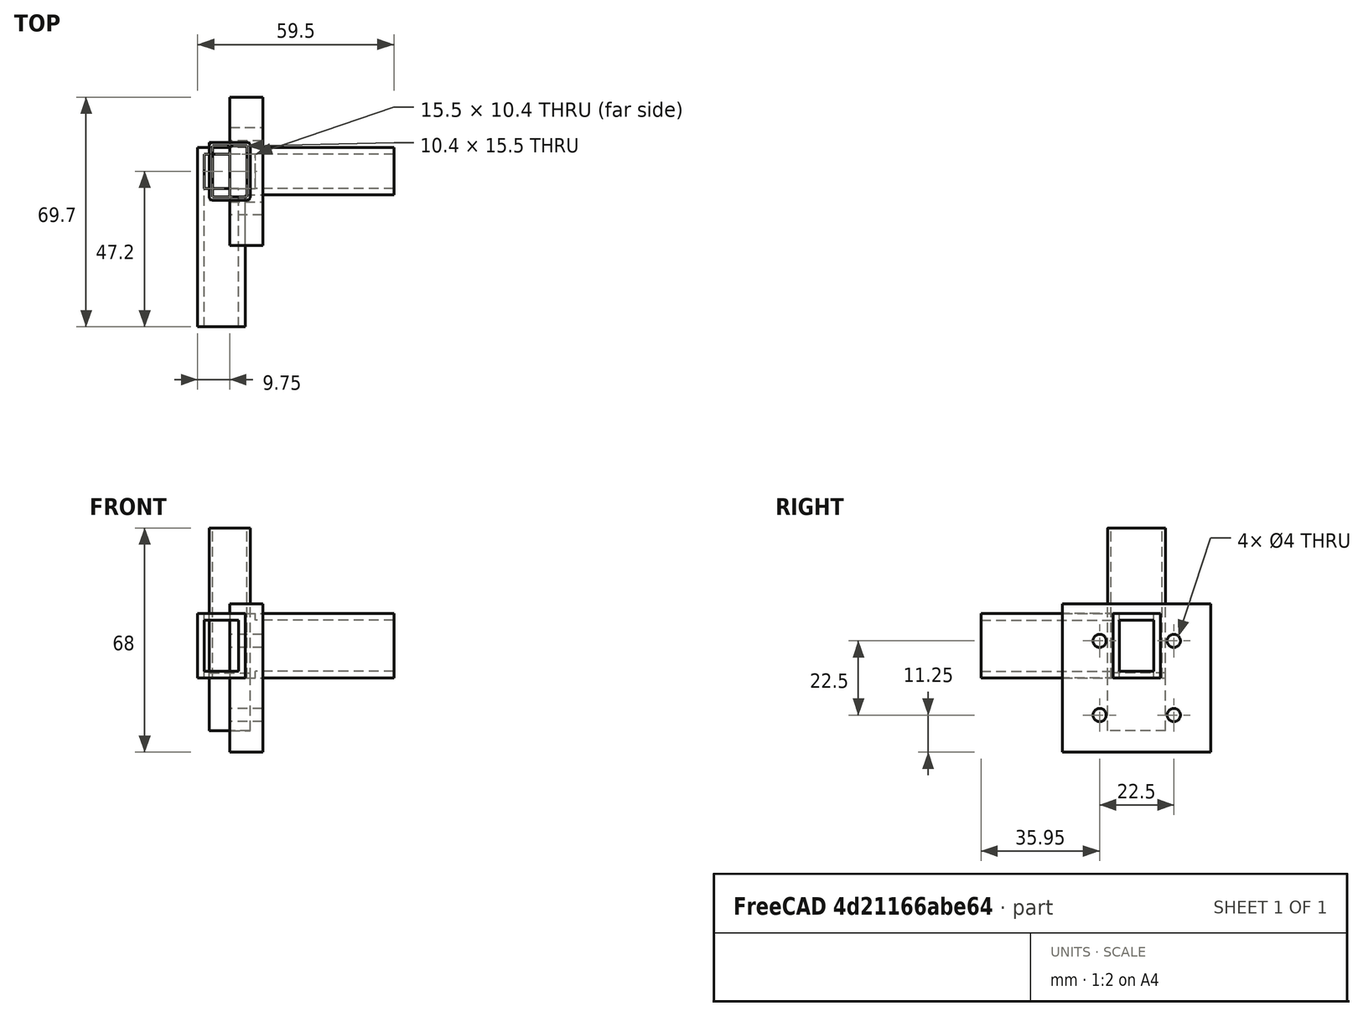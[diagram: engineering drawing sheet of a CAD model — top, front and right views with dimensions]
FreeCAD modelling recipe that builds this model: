
FCSTD DOCUMENT  (FreeCAD 2024.2R37179 (Git))
Label: Joints
License: All rights reserved
LicenseURL: https://en.wikipedia.org/wiki/All_rights_reserved
objects: Sketcher::SketchObject×7, App::Link×5, App::FeaturePython×5, PartDesign::Pad×4, PartDesign::Body×4, PartDesign::Pocket×2, Spreadsheet::Sheet×1, Assembly::JointGroup×1, Assembly::AssemblyObject×1
note: 23 computed .brp shape members not serialized (recipe doc carries the construction recipe); baked Part::Feature solids carry a one-line shape summary decoded from their .brp

FEATURE [Sketcher::SketchObject] Sketch
  AttachmentSupport = -> [XY_Plane]
  FullyConstrained = true
  MapMode = 5
  expr: Constraints[10] = Spreadsheet.width
  expr: Constraints[33] = Spreadsheet.height + Spreadsheet.thickness
  expr: Constraints[34] = Spreadsheet.width + Spreadsheet.thickness
  expr: Constraints[35] = Spreadsheet.diameter
  expr: Constraints[9] = Spreadsheet.height
  sketch-geometry (16):
    g0: LineSegment StartX=-5.2 StartY=-7.75 StartZ=0 EndX=5.2 EndY=-7.75 EndZ=0
    g1: LineSegment StartX=5.2 StartY=-7.75 StartZ=0 EndX=5.2 EndY=7.75 EndZ=0
    g2: LineSegment StartX=5.2 StartY=7.75 StartZ=0 EndX=-5.2 EndY=7.75 EndZ=0
    g3: LineSegment StartX=-5.2 StartY=7.75 StartZ=0 EndX=-5.2 EndY=-7.75 EndZ=0
    g4: GeomPoint X=0 Y=0 Z=0
    g5: LineSegment StartX=-6.2 StartY=7.75 StartZ=0 EndX=-6.2 EndY=-7.75 EndZ=0
    g6: LineSegment StartX=-5.2 StartY=-8.75 StartZ=0 EndX=5.2 EndY=-8.75 EndZ=0
    g7: LineSegment StartX=6.2 StartY=-7.75 StartZ=0 EndX=6.2 EndY=7.75 EndZ=0
    g8: LineSegment StartX=5.2 StartY=8.75 StartZ=0 EndX=-5.2 EndY=8.75 EndZ=0
    g9: ArcOfCircle CenterX=-5.2 CenterY=7.75 CenterZ=0 NormalX=0 NormalY=0 NormalZ=1 AngleXU=0 Radius=1 StartAngle=1.5708 EndAngle=3.14159
    g10: ArcOfCircle CenterX=-5.2 CenterY=-7.75 CenterZ=0 NormalX=0 NormalY=0 NormalZ=1 AngleXU=0 Radius=1 StartAngle=3.14159 EndAngle=4.71239
    g11: ArcOfCircle CenterX=5.2 CenterY=-7.75 CenterZ=0 NormalX=0 NormalY=0 NormalZ=1 AngleXU=0 Radius=1 StartAngle=4.71239 EndAngle=6.28319
    g12: ArcOfCircle CenterX=5.2 CenterY=7.75 CenterZ=0 NormalX=0 NormalY=0 NormalZ=1 AngleXU=0 Radius=1 StartAngle=2e-16 EndAngle=1.5708
    g13: GeomPoint X=-6.2 Y=8.75 Z=0
    g14: GeomPoint X=6.2 Y=-8.75 Z=0
    g15: GeomPoint X=0 Y=0 Z=0
  constraints (36):
    c: Coincident(g0,g1)
    c: Coincident(g1,g2)
    c: Coincident(g2,g3)
    c: Coincident(g3,g0)
    c: Horizontal(g0)
    c: Horizontal(g2)
    c: Vertical(g1)
    c: Vertical(g3)
    c: Symmetric(g2,g0,g4)
    c: Distance(g1,g3) = 10.4
    c: Distance(g0,g2) = 15.5
    c: Coincident(g4,g-1)
    c: Tangent(g5,g9) = -1.5708
    c: Tangent(g5,g10) = -1.5708
    c: Tangent(g6,g10) = -1.5708
    c: Tangent(g6,g11) = -1.5708
    c: Tangent(g7,g11) = -1.5708
    c: Tangent(g7,g12) = -1.5708
    c: Tangent(g8,g12) = -1.5708
    c: Tangent(g8,g9) = -1.5708
    c: Vertical(g5)
    c: Vertical(g7)
    c: Horizontal(g6)
    c: Horizontal(g8)
    c: Equal(g9,g10)
    c: Equal(g10,g11)
    c: Equal(g11,g12)
    c: PointOnObject(g13,g5)
    c: PointOnObject(g13,g8)
    c: PointOnObject(g14,g6)
    c: PointOnObject(g14,g7)
    c: Symmetric(g6,g8,g15)
    c: Coincident(g15,g4)
    c: Distance(g5,g7) = 12.4
    c: DistanceY(g6,g8) = 17.5
    c: Diameter(g12) = 2
FEATURE [Spreadsheet::Sheet] Spreadsheet
  cells = A1='width; B1(width)=15.5; A2='height; B2(height)=10.4; A3='thickness; B3(thickness)=2; A4='diameter; B4(diameter)=2
FEATURE [PartDesign::Pad] Pad
  Direction = (0,0,1)
  Length = 45.5
  Length2 = 10
  Profile = -> Sketch
  ReferenceAxis = -> Sketch [N_Axis]
  Refine = true
  Suppressed = false
  Type = 0
  expr: Length = Spreadsheet.width + 30
FEATURE [App::Link] Body001
  LinkPlacement = pos=(21.0202,-18.7098,9.0675) rot=(1,0,0;1.5708rad)
  LinkedObject = -> Body
  Placement = pos=(21.0202,-18.7098,9.0675) rot=(1,0,0;1.5708rad)
FEATURE [App::Link] Body002
  LinkPlacement = pos=(21.0202,-9.95982,63.3175) rot=(1,0,0;3.14159rad)
  LinkedObject = -> Body
  Placement = pos=(21.0202,-9.95982,63.3175) rot=(1,0,0;3.14159rad)
FEATURE [App::Link] Body003
  LinkPlacement = pos=(27.2202,-7.40981,9.06751) rot=(0.57735,0.57735,0.57735;2.0944rad)
  LinkedObject = -> Body
  Placement = pos=(27.2202,-7.40981,9.06751) rot=(0.57735,0.57735,0.57735;2.0944rad)
FEATURE [Sketcher::SketchObject] Sketch001
  AttachmentSupport = -> [Pad]
  FullyConstrained = true
  MapMode = 5
  Placement = pos=(0,0,45.5) rot=(0,0,1;0rad)
  expr: Constraints[10] = Spreadsheet.height + Spreadsheet.thickness
  expr: Constraints[11] = Spreadsheet.width + Spreadsheet.thickness
  sketch-geometry (5):
    g0: LineSegment StartX=-6.2 StartY=8.75 StartZ=0 EndX=-6.2 EndY=-8.75 EndZ=0
    g1: LineSegment StartX=-6.2 StartY=-8.75 StartZ=0 EndX=6.2 EndY=-8.75 EndZ=0
    g2: LineSegment StartX=6.2 StartY=-8.75 StartZ=0 EndX=6.2 EndY=8.75 EndZ=0
    g3: LineSegment StartX=6.2 StartY=8.75 StartZ=0 EndX=-6.2 EndY=8.75 EndZ=0
    g4: GeomPoint X=0 Y=0 Z=0
  constraints (12):
    c: Coincident(g0,g1)
    c: Coincident(g1,g2)
    c: Coincident(g2,g3)
    c: Coincident(g3,g0)
    c: Vertical(g0)
    c: Vertical(g2)
    c: Horizontal(g1)
    c: Horizontal(g3)
    c: Symmetric(g2,g0,g4)
    c: Coincident(g4,g-1)
    c: Distance(g3,g3) = 12.4
    c: DistanceY(g2,g2) = 17.5
FEATURE [PartDesign::Body] Body
  Group = -> [Sketch,Pad,Sketch001]
  Origin = -> Origin
  Tip = -> Pad
FEATURE [App::FeaturePython] GroundedJoint  # Assembly grounded joint (typed FeaturePython)
  ObjectToGround = -> Body002
  Placement = pos=(21.0202,-9.95982,63.3175) rot=(1,0,0;3.14159rad)
FEATURE [App::FeaturePython] Fixed  # Assembly joint (typed FeaturePython)
  Activated = true
  AngleMax = 0
  AngleMin = 0
  Detach1 = false
  Detach2 = false
  Distance = 0
  Distance2 = 0
  Element1 = Edge22
  Element2 = Edge21
  EnableLimits = false
  JointType = 0 (Fixed)
  LengthMax = 0
  LengthMin = 0
  Object1 = Body002
  Object2 = Body001
  Offset = (0,0,0)
  Part1 = -> Body002
  Part2 = -> Body001
  Placement1 = pos=(-3.6e-15,8.75,45.5) rot=(-0.707107,0,0.707107;3.14159rad)
  Placement2 = pos=(0,8.75,0) rot=(0.57735,0.57735,-0.57735;4.18879rad)
  Rotation = -90
  Vertex1 = Edge22
  Vertex2 = Edge21
FEATURE [Sketcher::SketchObject] Sketch002
  AttachmentSupport = -> [XY_Plane002]
  FullyConstrained = true
  MapMode = 5
  expr: Constraints[10] = Spreadsheet.height + Spreadsheet.thickness
  expr: Constraints[11] = Spreadsheet.width + Spreadsheet.thickness
  sketch-geometry (5):
    g0: LineSegment StartX=-6.2 StartY=8.75 StartZ=0 EndX=-6.2 EndY=-8.75 EndZ=0
    g1: LineSegment StartX=-6.2 StartY=-8.75 StartZ=0 EndX=6.2 EndY=-8.75 EndZ=0
    g2: LineSegment StartX=6.2 StartY=-8.75 StartZ=0 EndX=6.2 EndY=8.75 EndZ=0
    g3: LineSegment StartX=6.2 StartY=8.75 StartZ=0 EndX=-6.2 EndY=8.75 EndZ=0
    g4: GeomPoint X=0 Y=0 Z=0
  constraints (12):
    c: Coincident(g0,g1)
    c: Coincident(g1,g2)
    c: Coincident(g2,g3)
    c: Coincident(g3,g0)
    c: Vertical(g0)
    c: Vertical(g2)
    c: Horizontal(g1)
    c: Horizontal(g3)
    c: Symmetric(g2,g0,g4)
    c: Coincident(g4,g-1)
    c: Distance(g3,g3) = 12.4
    c: DistanceY(g2,g2) = 17.5
FEATURE [PartDesign::Pad] Pad001
  Direction = (0,0,1)
  Length = 17.5
  Length2 = 10
  Profile = -> Sketch002
  ReferenceAxis = -> Sketch002 [N_Axis]
  Refine = true
  Suppressed = false
  Type = 0
  expr: Length = Spreadsheet.thickness + Spreadsheet.width
FEATURE [PartDesign::Body] Body004
  Group = -> [Sketch002,Pad001]
  Origin = -> Origin002
  Placement = pos=(0,0,-16) rot=(0,0,1;0rad)
  Tip = -> Pad001
FEATURE [App::Link] Body005
  LinkPlacement = pos=(21.0202,-9.95981,0.317505) rot=(0.99808,0,0;0rad)
  LinkedObject = -> Body004
  Placement = pos=(21.0202,-9.95981,0.317505) rot=(0.99808,0,0;0rad)
FEATURE [App::FeaturePython] Fixed001  # Assembly joint (typed FeaturePython)
  Activated = true
  AngleMax = 0
  AngleMin = 0
  Detach1 = false
  Detach2 = false
  Distance = 0
  Distance2 = 0
  Element1 = Edge4
  Element2 = Edge4
  EnableLimits = false
  JointType = 0 (Fixed)
  LengthMax = 0
  LengthMin = 0
  Object1 = Body005
  Object2 = Body002
  Offset = (0,0,0)
  Part1 = -> Body005
  Part2 = -> Body002
  Placement1 = pos=(-6.2,-1.8e-15,17.5) rot=(-0.57735,-0.57735,0.57735;4.18879rad)
  Placement2 = pos=(-6.2,1.8e-15,45.5) rot=(-0.57735,0.57735,-0.57735;4.18879rad)
  Rotation = 180
  Vertex1 = Edge4
  Vertex2 = Edge4
FEATURE [App::FeaturePython] Fixed002  # Assembly joint (typed FeaturePython)
  Activated = true
  AngleMax = 0
  AngleMin = 0
  Detach1 = false
  Detach2 = false
  Distance = 0
  Distance2 = 0
  Element1 = Edge8
  Element2 = Edge15
  EnableLimits = false
  JointType = 0 (Fixed)
  LengthMax = 0
  LengthMin = 0
  Object1 = Body005
  Object2 = Body003
  Offset = (0,0,0)
  Part1 = -> Body005
  Part2 = -> Body003
  Placement1 = pos=(6.2,8.75,8.75) rot=(0,0,1;0rad)
  Placement2 = pos=(6.2,0,0) rot=(0.57735,0.57735,0.57735;4.18879rad)
  Rotation = 0
  Vertex1 = Edge8
  Vertex2 = Edge15
FEATURE [Sketcher::SketchObject] Sketch003
  AttachmentSupport = -> [YZ_Plane003]
  FullyConstrained = true
  MapMode = 5
  Placement = pos=(0,0,0) rot=(0.57735,0.57735,0.57735;2.0944rad)
  sketch-geometry (10):
    g0: LineSegment StartX=-22.5 StartY=-22.5 StartZ=0 EndX=22.5 EndY=-22.5 EndZ=0
    g1: LineSegment StartX=22.5 StartY=-22.5 StartZ=0 EndX=22.5 EndY=22.5 EndZ=0
    g2: LineSegment StartX=22.5 StartY=22.5 StartZ=0 EndX=-22.5 EndY=22.5 EndZ=0
    g3: LineSegment StartX=-22.5 StartY=22.5 StartZ=0 EndX=-22.5 EndY=-22.5 EndZ=0
    g4: GeomPoint X=0 Y=0 Z=0
    g5: Circle CenterX=-11.25 CenterY=-11.25 CenterZ=0 NormalX=0 NormalY=0 NormalZ=1 AngleXU=0 Radius=2
    g6: Circle CenterX=11.25 CenterY=-11.25 CenterZ=0 NormalX=0 NormalY=0 NormalZ=1 AngleXU=0 Radius=2
    g7: Circle CenterX=11.25 CenterY=11.25 CenterZ=0 NormalX=0 NormalY=0 NormalZ=1 AngleXU=0 Radius=2
    g8: Circle CenterX=-11.25 CenterY=11.25 CenterZ=0 NormalX=0 NormalY=0 NormalZ=1 AngleXU=0 Radius=2
    g9: GeomPoint X=0 Y=0 Z=0
  constraints (23):
    c: Coincident(g0,g1)
    c: Coincident(g1,g2)
    c: Coincident(g2,g3)
    c: Coincident(g3,g0)
    c: Horizontal(g0)
    c: Horizontal(g2)
    c: Vertical(g1)
    c: Vertical(g3)
    c: Symmetric(g2,g0,g4)
    c: Distance(g1,g3) = 45
    c: Distance(g0,g2) = 45
    c: Coincident(g4,g-1)
    c: Equal(g8,g7)
    c: Equal(g7,g6)
    c: Equal(g6,g5)
    c: Horizontal(g8,g7)
    c: Horizontal(g5,g6)
    c: Vertical(g8,g5)
    c: Vertical(g7,g6)
    c: Symmetric(g5,g7,g9)
    c: Coincident(g9,g4)
    c: Diameter(g7) = 4
    c: Symmetric(g4,g1,g7)
FEATURE [PartDesign::Pad] Pad002
  Direction = (1,0,0)
  Length = 10
  Length2 = 10
  Placement = pos=(0,0,0) rot=(1,1,1;2.0944rad)
  Profile = -> Sketch003
  ReferenceAxis = -> Sketch003 [N_Axis]
  Refine = true
  Suppressed = false
  Type = 0
  expr: Length = 10 mm
FEATURE [PartDesign::Body] Body006
  Group = -> [Sketch003,Pad002]
  Origin = -> Origin003
  Tip = -> Pad002
FEATURE [App::Link] Body007
  LinkPlacement = pos=(49.7202,-35.1098,10.3175) rot=(0,1,0;1.5708rad)
  LinkedObject = -> Body006
  Placement = pos=(49.7202,-35.1098,10.3175) rot=(0,1,0;1.5708rad)
FEATURE [App::FeaturePython] Fixed003  # Assembly joint (typed FeaturePython)
  Activated = true
  AngleMax = 0
  AngleMin = 0
  Detach1 = false
  Detach2 = false
  Distance = 0
  Distance2 = 0
  Element1 = Vertex5
  Element2 = Vertex4
  EnableLimits = false
  JointType = 0 (Fixed)
  LengthMax = 0
  LengthMin = 0
  Object1 = Body003
  Object2 = Body007
  Offset = (0,0,0)
  Part1 = -> Body003
  Part2 = -> Body007
  Placement1 = pos=(-5.2,-8.75,0) rot=(0,0,1;0rad)
  Placement2 = pos=(10,22.5,-22.5) rot=(0,0,1;1.5708rad)
  Rotation = 90
  Vertex1 = Vertex5
  Vertex2 = Vertex4
FEATURE [Assembly::JointGroup] Joints
  Group = -> [GroundedJoint,Fixed,Fixed001,Fixed002,Fixed003]
FEATURE [Assembly::AssemblyObject] Assembly
  Group = -> [Joints,Body001,Body002,Body003,GroundedJoint,Fixed,Body005,Fixed001,Fixed002,Body007,Fixed003]
  Origin = -> Origin001
  Type = Assembly
FEATURE [Sketcher::SketchObject] Sketch004
  AttachmentSupport = -> [XY_Plane004]
  FullyConstrained = true
  MapMode = 5
  expr: Constraints[10] = Spreadsheet.width
  expr: Constraints[11] = Spreadsheet.height
  expr: Constraints[24] = Spreadsheet.thickness
  expr: Constraints[25] = Spreadsheet.thickness
  expr: Constraints[26] = Spreadsheet.thickness
  expr: Constraints[29] = Spreadsheet.height + 2 * Spreadsheet.thickness
  sketch-geometry (11):
    g0: LineSegment StartX=-7.75 StartY=5.2 StartZ=0 EndX=-7.75 EndY=-5.2 EndZ=0
    g1: LineSegment StartX=-7.75 StartY=-5.2 StartZ=0 EndX=7.75 EndY=-5.2 EndZ=0
    g2: LineSegment StartX=7.75 StartY=-5.2 StartZ=0 EndX=7.75 EndY=5.2 EndZ=0
    g3: LineSegment StartX=7.75 StartY=5.2 StartZ=0 EndX=-7.75 EndY=5.2 EndZ=0
    g4: GeomPoint X=0 Y=0 Z=0
    g5: LineSegment StartX=-9.75 StartY=7.2 StartZ=0 EndX=-9.75 EndY=-47.2 EndZ=0
    g6: LineSegment StartX=-9.75 StartY=-47.2 StartZ=0 EndX=4.65 EndY=-47.2 EndZ=0
    g7: LineSegment StartX=4.65 StartY=-47.2 StartZ=0 EndX=4.65 EndY=-7.2 EndZ=0
    g8: LineSegment StartX=4.65 StartY=-7.2 StartZ=0 EndX=49.75 EndY=-7.2 EndZ=0
    g9: LineSegment StartX=49.75 StartY=-7.2 StartZ=0 EndX=49.75 EndY=7.2 EndZ=0
    g10: LineSegment StartX=49.75 StartY=7.2 StartZ=0 EndX=-9.75 EndY=7.2 EndZ=0
  constraints (30):
    c: Coincident(g0,g1)
    c: Coincident(g1,g2)
    c: Coincident(g2,g3)
    c: Coincident(g3,g0)
    c: Vertical(g0)
    c: Vertical(g2)
    c: Horizontal(g1)
    c: Horizontal(g3)
    c: Symmetric(g2,g0,g4)
    c: Coincident(g4,g-1)
    c: Distance(g3,g3) = 15.5
    c: DistanceY(g2,g2) = 10.4
    c: Vertical(g5)
    c: Coincident(g5,g6)
    c: Horizontal(g6)
    c: Coincident(g6,g7)
    c: Vertical(g7)
    c: Coincident(g7,g8)
    c: Horizontal(g8)
    c: Coincident(g8,g9)
    c: Vertical(g9)
    c: Coincident(g9,g10)
    c: Coincident(g10,g5)
    c: Horizontal(g10)
    c: DistanceY(g0,g5) = 2
    c: DistanceX(g5,g0) = 2
    c: DistanceY(g7,g1) = 2
    c: DistanceX(g2,g9) = 42
    c: DistanceY(g5,g0) = 42
    c: DistanceX(g6,g6) = 14.4
FEATURE [PartDesign::Pad] Pad003
  Direction = (0,0,1)
  Length = 19.5
  Length2 = 10
  Profile = -> Sketch004
  ReferenceAxis = -> Sketch004 [N_Axis]
  Refine = true
  Suppressed = false
  Type = 0
  expr: Length = Spreadsheet.width + 2 * Spreadsheet.thickness
FEATURE [Sketcher::SketchObject] Sketch005
  AttachmentSupport = -> [Pad003]
  ExternalGeometry = -> [Pad003]
  FullyConstrained = true
  MapMode = 5
  Placement = pos=(0,-47.2,0) rot=(1,0,0;1.5708rad)
  expr: Constraints[10] = Spreadsheet.width
  expr: Constraints[11] = Spreadsheet.thickness
  expr: Constraints[12] = Spreadsheet.thickness
  expr: Constraints[9] = Spreadsheet.height
  sketch-geometry (5):
    g0: LineSegment StartX=-7.75 StartY=17.5 StartZ=0 EndX=-7.75 EndY=2 EndZ=0
    g1: LineSegment StartX=-7.75 StartY=2 StartZ=0 EndX=2.65 EndY=2 EndZ=0
    g2: LineSegment StartX=2.65 StartY=2 StartZ=0 EndX=2.65 EndY=17.5 EndZ=0
    g3: LineSegment StartX=2.65 StartY=17.5 StartZ=0 EndX=-7.75 EndY=17.5 EndZ=0
    g4: GeomPoint X=-2.55 Y=9.75 Z=0
  constraints (13):
    c: Coincident(g0,g1)
    c: Coincident(g1,g2)
    c: Coincident(g2,g3)
    c: Coincident(g3,g0)
    c: Vertical(g0)
    c: Vertical(g2)
    c: Horizontal(g1)
    c: Horizontal(g3)
    c: Symmetric(g2,g0,g4)
    c: Distance(g3,g3) = 10.4
    c: DistanceY(g2,g2) = 15.5
    c: DistanceX(g1,g-4) = 2
    c: DistanceY(g0,g-3) = 2
FEATURE [PartDesign::Pocket] Pocket
  BaseFeature = -> Pad003
  Direction = (0,1,-2e-16)
  Length = 45
  Length2 = 5
  Profile = -> Sketch005
  ReferenceAxis = -> Sketch005 [N_Axis]
  Refine = true
  Suppressed = false
  Type = 0
FEATURE [Sketcher::SketchObject] Sketch006
  AttachmentSupport = -> [Pocket]
  ExternalGeometry = -> [Pocket]
  FullyConstrained = true
  MapMode = 5
  Placement = pos=(49.75,0,0) rot=(0.57735,0.57735,0.57735;2.0944rad)
  expr: Constraints[10] = Spreadsheet.width
  expr: Constraints[11] = Spreadsheet.thickness
  expr: Constraints[12] = Spreadsheet.thickness
  expr: Constraints[9] = Spreadsheet.height
  sketch-geometry (5):
    g0: LineSegment StartX=-5.2 StartY=17.5 StartZ=0 EndX=-5.2 EndY=2 EndZ=0
    g1: LineSegment StartX=-5.2 StartY=2 StartZ=0 EndX=5.2 EndY=2 EndZ=0
    g2: LineSegment StartX=5.2 StartY=2 StartZ=0 EndX=5.2 EndY=17.5 EndZ=0
    g3: LineSegment StartX=5.2 StartY=17.5 StartZ=0 EndX=-5.2 EndY=17.5 EndZ=0
    g4: GeomPoint X=-1.1e-15 Y=9.75 Z=0
  constraints (13):
    c: Coincident(g0,g1)
    c: Coincident(g1,g2)
    c: Coincident(g2,g3)
    c: Coincident(g3,g0)
    c: Vertical(g0)
    c: Vertical(g2)
    c: Horizontal(g1)
    c: Horizontal(g3)
    c: Symmetric(g2,g0,g4)
    c: Distance(g3,g3) = 10.4
    c: DistanceY(g2,g2) = 15.5
    c: DistanceX(g2,g-4) = 2
    c: DistanceY(g2,g-4) = 2
FEATURE [PartDesign::Pocket] Pocket001
  BaseFeature = -> Pocket
  Direction = (-1,0,0)
  Length = 45
  Length2 = 5
  Profile = -> Sketch006
  ReferenceAxis = -> Sketch006 [N_Axis]
  Refine = true
  Suppressed = false
  Type = 0
FEATURE [PartDesign::Body] Body008
  Group = -> [Sketch004,Pad003,Sketch005,Pocket,Sketch006,Pocket001]
  Origin = -> Origin004
  Tip = -> Pocket001
